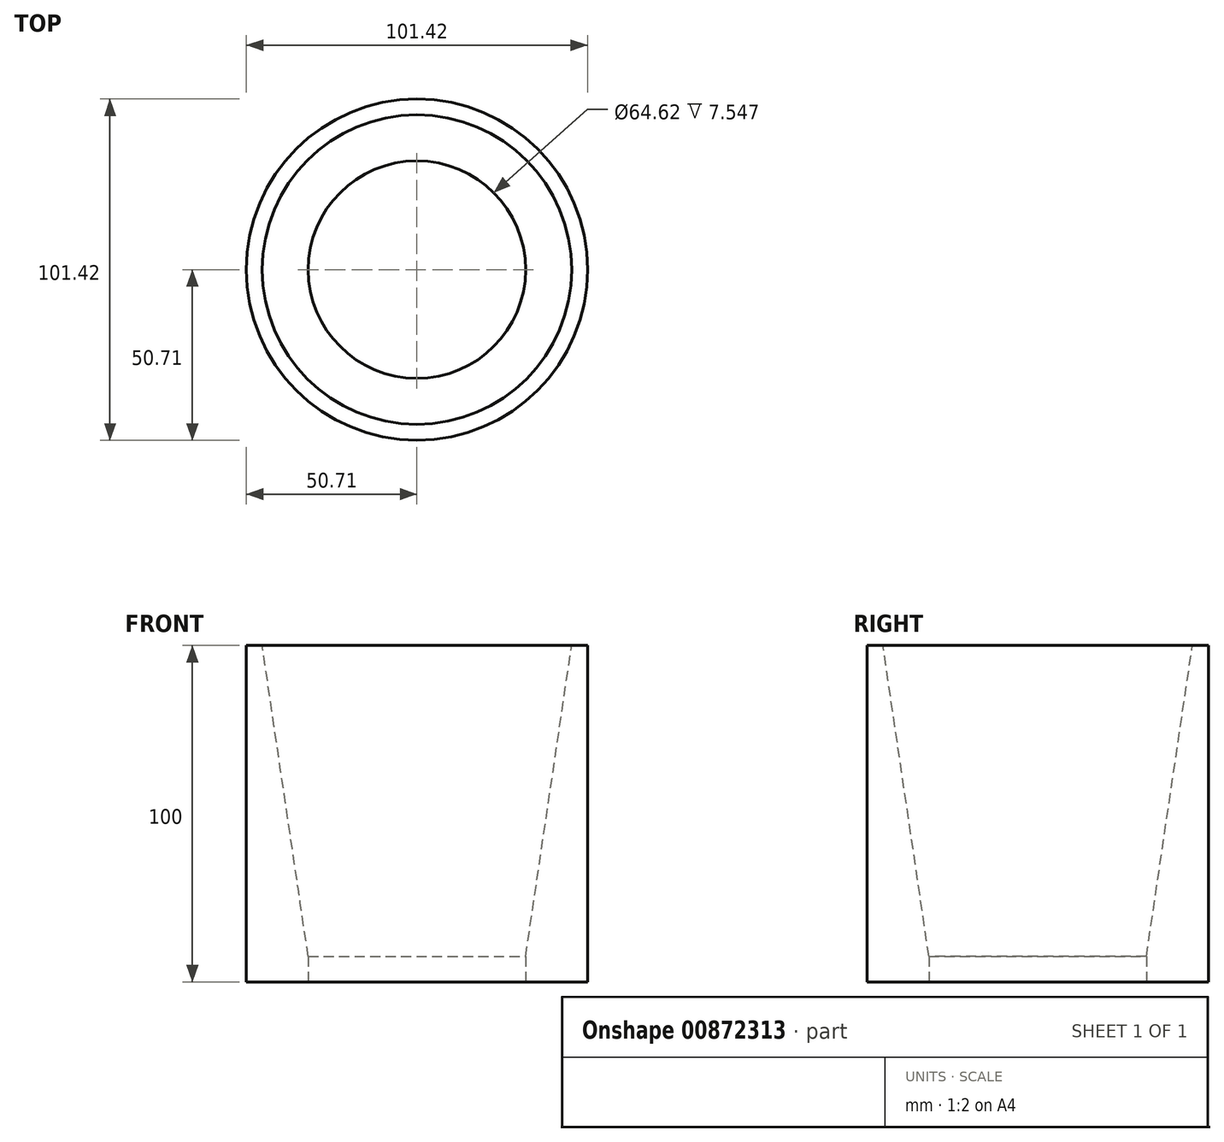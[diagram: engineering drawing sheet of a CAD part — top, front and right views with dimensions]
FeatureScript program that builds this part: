
annotation { "Feature Type Name" : "Feature", "Feature Type Description" : "" }
export const myFeature = defineFeature(function(context is Context, id is Id, definition is map)
    precondition{}
    {
        {
            var Q0;
            Q0=qCreatedBy(makeId("Front.planeOp"),FACE);
            var sketch = newSketch(context, id + "F0", { "sketchPlane" : qUnion([Q0])});
            skLineSegment(sketch, "E0", {"start": v(0, 0) * mm, "end": v(0, 100) * mm, "construction": true});
            skLineSegment(sketch, "E1", {"start": v(50.7, 0) * mm, "end": v(50.7, 100) * mm});
            skLineSegment(sketch, "E2", {"start": v(50.7, 100) * mm, "end": v(46, 100) * mm});
            skLineSegment(sketch, "E3", {"start": v(46, 100) * mm, "end": v(32.31, 7.55) * mm});
            skLineSegment(sketch, "E4", {"start": v(32.31, 7.55) * mm, "end": v(32.31, 0) * mm});
            skLineSegment(sketch, "E5", {"start": v(32.31, 0) * mm, "end": v(50.7, 0) * mm});
            skSolve(sketch);
        }
        {
            var Q0;
            Q0=makeQuery(id+"F0.imprint","IMPRINT",FACE,{"disambiguationData":[TD([[makeQuery(id+"F0.imprint","IMPRINT",EDGE,{"derivedFrom":sQuery(id+"F0.wireOp",EDGE,"E1")}),1.0]])]});
            var Q1;
            Q1=sQuery(id+"F0.wireOp",EDGE,"E0");
            revolve(context, id + "F1", {"surfaceOperationType" : NewSurfaceOperationType.NEW, "entities" : qUnion([Q0]), "axis" : qUnion([Q1]), "revolveType" : RevolveType.FULL});
        }
    });
